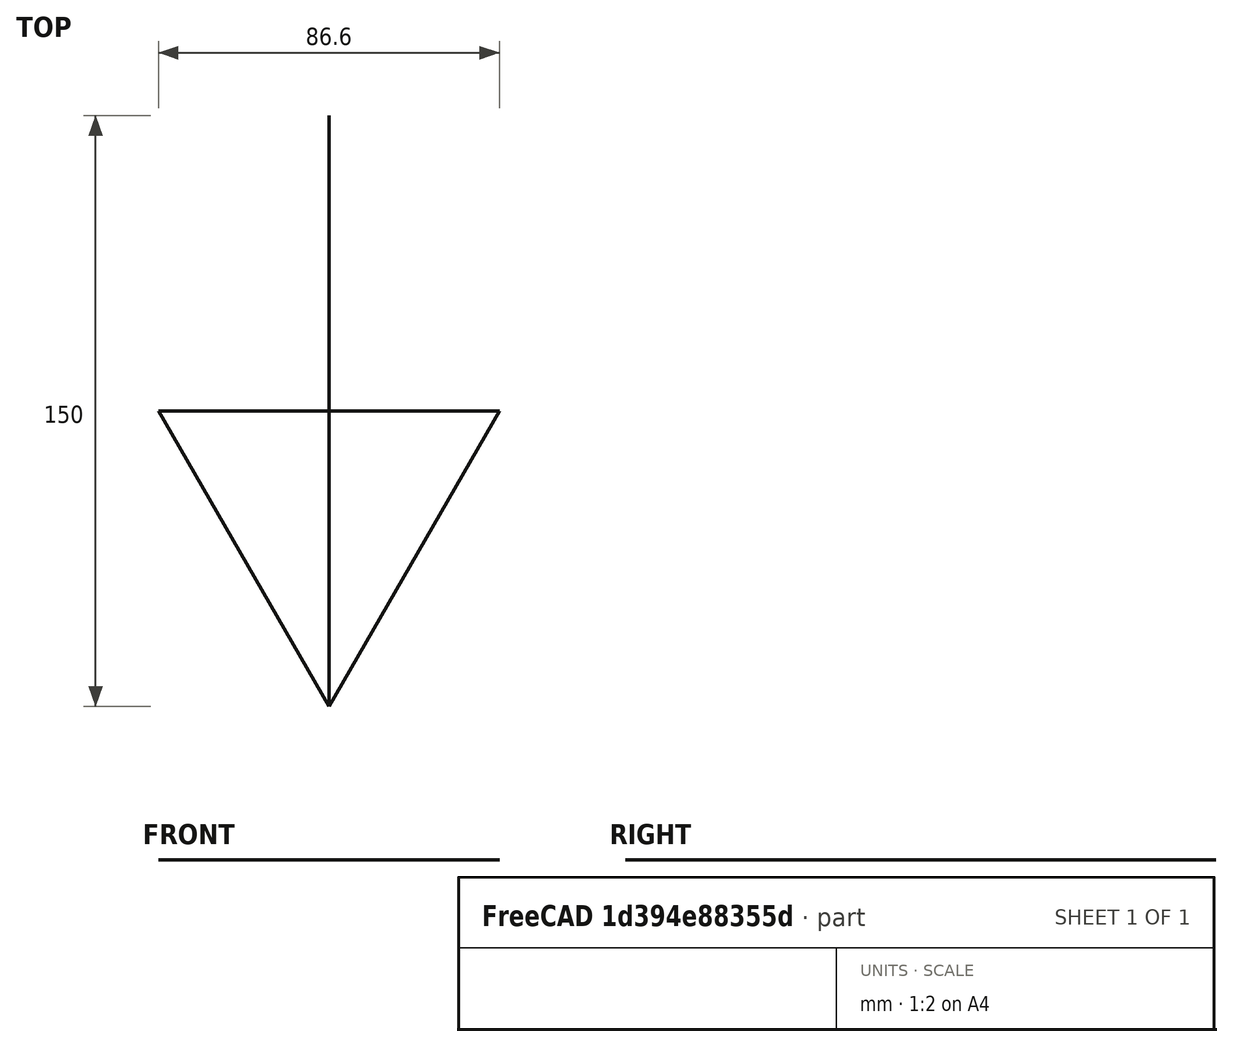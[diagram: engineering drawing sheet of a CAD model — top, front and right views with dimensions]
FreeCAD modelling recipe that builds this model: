
FCSTD DOCUMENT  (FreeCAD 1.1R20260325 (Git shallow))
Label: Tomada_Media_1modulo_110v_com_simbologia
License: All rights reserved
LicenseURL: http://en.wikipedia.org/wiki/All_rights_reserved
objects: Part::FeaturePython×1, Part::Feature×1, App::DocumentObjectGroup×1
note: 2 computed .brp shape members not serialized (recipe doc carries the construction recipe); baked Part::Feature solids carry a one-line shape summary decoded from their .brp

FEATURE [Part::FeaturePython] Component  label="Tomada_1modulo_110v"  # Arch/BIM 0 (typed FeaturePython)
  HorizontalArea = 0
  IfcData = attributes={"GlobalId": {"name": "GlobalId", "type": "IfcGloballyUniqueId", "is_enum": false, "enum_values": []}, "Description": {"... (+538 chars omitted),+1 more (map truncated)
  IfcType = 0
  MoveBase = false
  MoveWithHost = false
  PerimeterLength = 0
  Placement = pos=(0,0,1200) rot=(0,0,1;0rad)
  PredefinedType = 0
  VerticalArea = 0
FEATURE [Part::Feature] Compound002002002004005002002003003002003005002002005002002002002002002002002002002001  label="Simbologia_Tomada_Media"
  Placement = pos=(871.053,2055.85,1190.37) rot=(0,0,-1;1.5708rad)
  shape: bbox 86.6 x 150 x 2e-07 mm, 1 faces, 0 solids (baked)
FEATURE [App::DocumentObjectGroup] Group  label="Tomada_1modulo_Media"
  Group = -> [Component,Compound002002002004005002002003003002003005002002005002002002002002002002002002002001]
